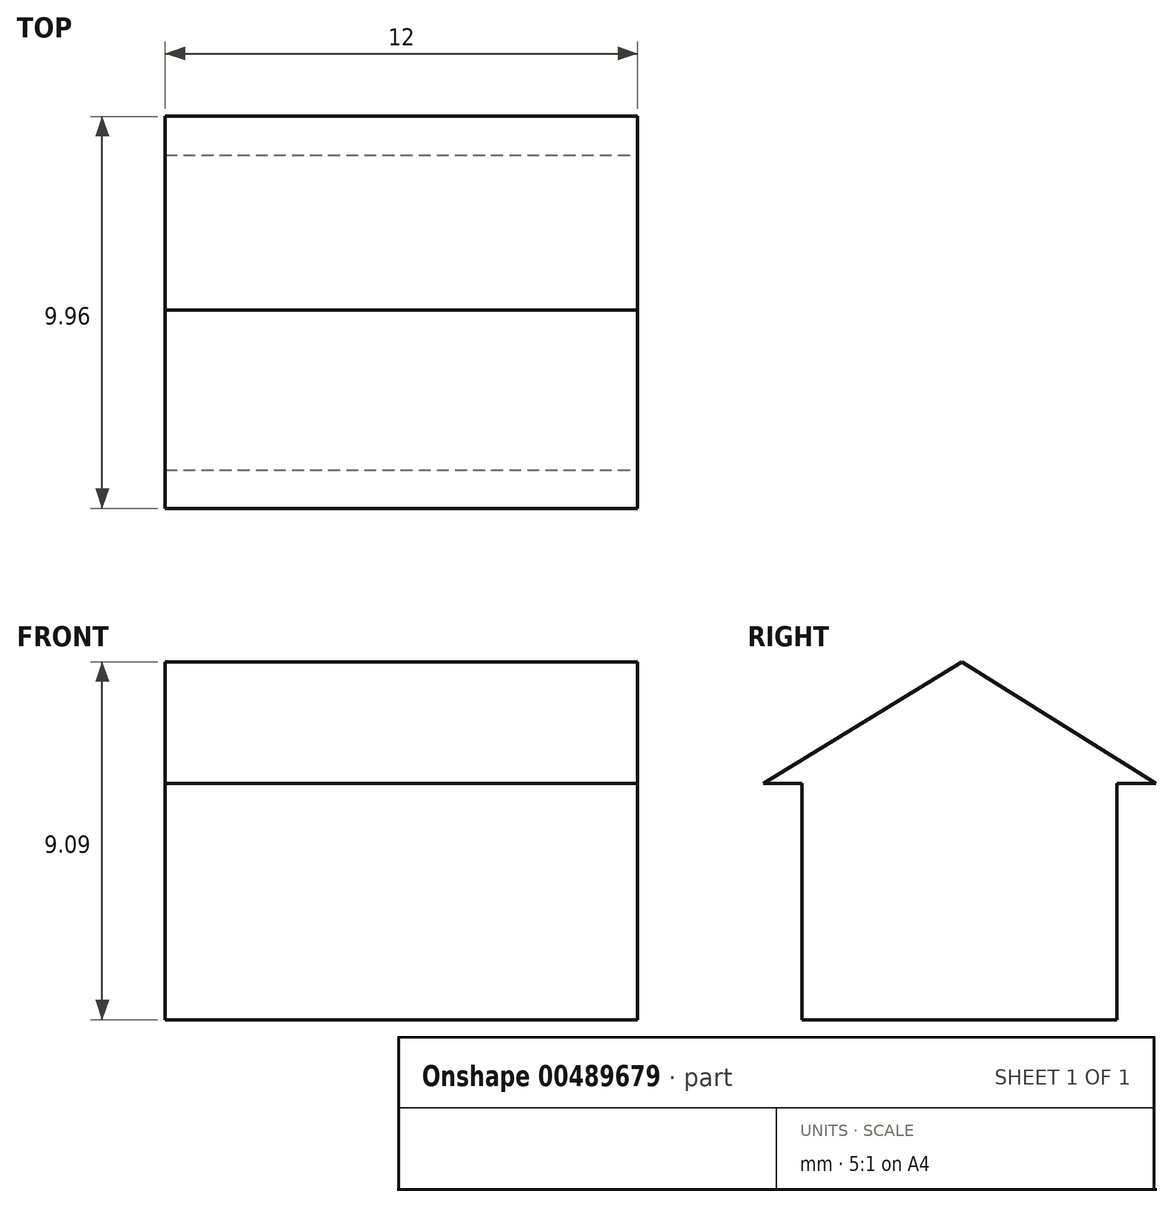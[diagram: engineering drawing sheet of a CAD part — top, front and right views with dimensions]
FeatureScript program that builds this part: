
annotation { "Feature Type Name" : "Feature", "Feature Type Description" : "" }
export const myFeature = defineFeature(function(context is Context, id is Id, definition is map)
    precondition{}
    {
        {
            var Q0;
            Q0=qCreatedBy(makeId("Top.planeOp"),FACE);
            var sketch = newSketch(context, id + "F0", { "sketchPlane" : qUnion([Q0])});
            skLineSegment(sketch, "E0.bottom", {"start": v(-6.5, 8) * mm, "end": v(5.5, 8) * mm});
            skLineSegment(sketch, "E0.top", {"start": v(-6.5, 0) * mm, "end": v(5.5, 0) * mm});
            skLineSegment(sketch, "E0.left", {"start": v(-6.5, 8) * mm, "end": v(-6.5, 0) * mm});
            skLineSegment(sketch, "E0.right", {"start": v(5.5, 8) * mm, "end": v(5.5, 0) * mm});
            skSolve(sketch);
        }
        {
            var Q0;
            Q0=makeQuery(id+"F0.imprint","IMPRINT",FACE,{"disambiguationData":[TD([[makeQuery(id+"F0.imprint","IMPRINT",EDGE,{"derivedFrom":sQuery(id+"F0.wireOp",EDGE,"E0.bottom")}),-1.0]])]});
            extrude(context, id + "F1", {"entities" : qUnion([Q0]), "depth" : 6 * mm});
        }
        {
            var Q0;
            Q0=makeQuery(id+"F1.opExtrude","SWEPT_FACE",FACE,{"disambiguationData":[OSD([sQuery(id+"F0.wireOp",EDGE,"E0.left")])]});
            var sketch = newSketch(context, id + "F2", { "sketchPlane" : qUnion([Q0])});
            skLineSegment(sketch, "E1", {"start": v(-8.98, 6) * mm, "end": v(0.98, 6) * mm});
            skLineSegment(sketch, "E2", {"start": v(-8.98, 6) * mm, "end": v(-4.05, 9.1) * mm});
            skLineSegment(sketch, "E3", {"start": v(-4.05, 9.1) * mm, "end": v(0.98, 6) * mm});
            skLineSegment(sketch, "E4", {"start": v(-4.05, 9.1) * mm, "end": v(-4.05, -0.84) * mm, "construction": true});
            skSolve(sketch);
        }
        {
            var Q0;
            {var subQ0=sQuery(id+"F2.wireOp",EDGE,"E2");Q0=makeQuery(id+"F2.imprint","IMPRINT",FACE,{"disambiguationData":[TD([[makeQuery(id+"F2.imprint","IMPRINT",EDGE,{"derivedFrom":subQ0}),-1.0]])]});}
            extrude(context, id + "F3", {"entities" : qUnion([Q0]), "operationType" : NewBodyOperationType.ADD, "oppositeDirection" : true, "depth" : 12 * mm});
        }
    });
